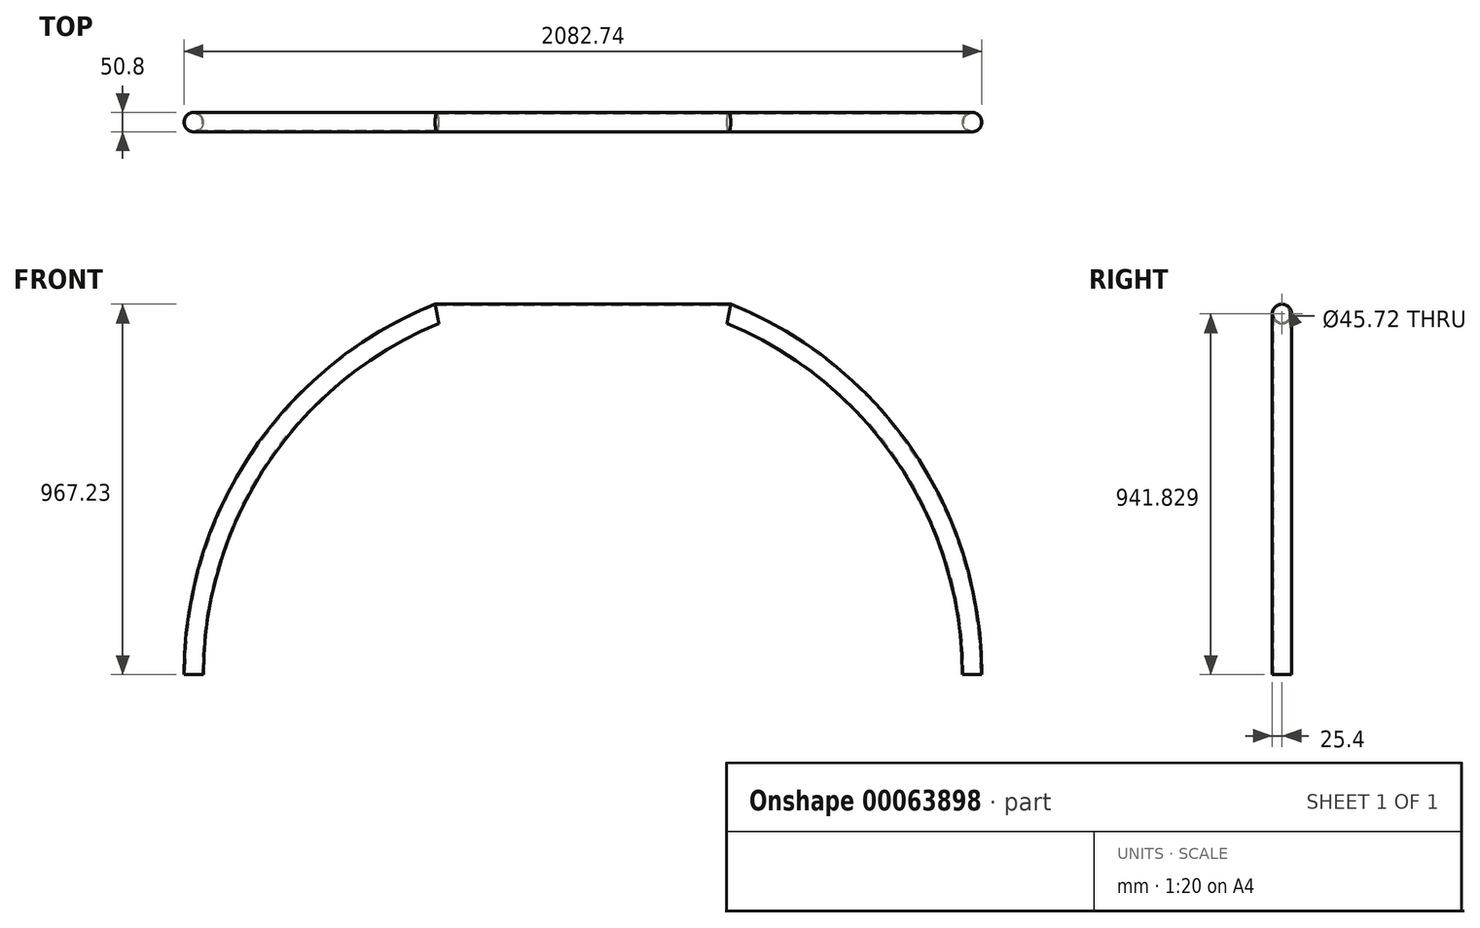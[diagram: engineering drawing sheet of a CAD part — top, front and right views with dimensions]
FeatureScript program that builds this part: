
annotation { "Feature Type Name" : "Feature", "Feature Type Description" : "" }
export const myFeature = defineFeature(function(context is Context, id is Id, definition is map)
    precondition{}
    {
        {
            var Q0;
            Q0=qCreatedBy(makeId("Front.planeOp"),FACE);
            var sketch = newSketch(context, id + "F0", { "sketchPlane" : qUnion([Q0])});
            skLineSegment(sketch, "E0", {"start": v(-1020.24, 0) * mm, "end": v(1011.76, 0) * mm, "construction": true});
            skArc(sketch, "E1", {"start": v(1011.76, 0) * mm, "mid": v(838.18, 567.96) * mm, "end": v(376.76, 941.86) * mm});
            skLineSegment(sketch, "E2", {"start": v(-385.24, 941.86) * mm, "end": v(376.76, 941.86) * mm});
            skArc(sketch, "E3.trimOffspring", {"start": v(-385.24, 941.86) * mm, "mid": v(-846.66, 567.96) * mm, "end": v(-1020.24, 0) * mm});
            skSolve(sketch);
        }
        {
            var Q0;
            Q0=qCreatedBy(makeId("Top.planeOp"),FACE);
            var sketch = newSketch(context, id + "F1", { "sketchPlane" : qUnion([Q0])});
            skCircle(sketch, "E4", {"center": v(-1020.21, 0) * mm, "radius": 25.4 * mm});
            skCircle(sketch, "E5", {"center": v(-1020.21, 0) * mm, "radius": 22.86 * mm});
            skSolve(sketch);
        }
        {
            var Q0;
            Q0=makeQuery(id+"F1.imprint","IMPRINT",FACE,{"disambiguationData":[TD([[makeQuery(id+"F1.imprint","IMPRINT",EDGE,{"derivedFrom":sQuery(id+"F1.wireOp",EDGE,"E4")}),1.0]])]});
            var Q1;
            Q1 = qConstructionFilter(qBodyType(qCreatedBy(id + "F0" ,EDGE), BodyType.WIRE), ConstructionObject.NO);
            sweep(context, id + "F2", {"profiles" : qUnion([Q0]), "path" : qUnion([Q1])});
        }
    });
